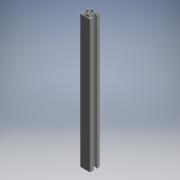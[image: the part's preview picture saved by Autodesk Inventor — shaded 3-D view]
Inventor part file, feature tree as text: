
AUTODESK INVENTOR PART (.ipt)
format: ipt  version: 2017.3 (Build 213256000, 256)  size: 203,264 bytes
history: native  units: mm (DEFAULTED — no unit token found)
features: other x7, sketch x2, extrude x1, hole x1
ambient origin geometry x8: Origin, YZ Plane, XZ Plane, XY Plane, X Axis, Y Axis, Z Axis, Center Point
bodies: Solid1 (feature_tree)
feature tree (11):
  extrude  "Extrusion1"  TaperAngle=0.0deg  [1 undecoded]
  hole  "Hole1"  [1 undecoded]
  other  "C1_XY"
  other  "C1_YZ"
  other  "C1_ZX"
  other  "C1_X"
  other  "C1_Y"
  other  "C1_Z"
  other  "C1_Center"
  sketch  "Sketch_76"  dims[d2=4.2mm d3=6.0mm d4=4.0mm d5=2.0mm d6=90.0deg d7=263.5mm d8=0.0mm d9=0.0mm]
  sketch  "Sketch2"  dims[d0=263.5mm d1=0.0mm]
note: 2 required parameter values undecoded (feature->parameter linkage not recoverable at this tier; creation-order binding heuristic only, values carry confidence <= 0.55)
